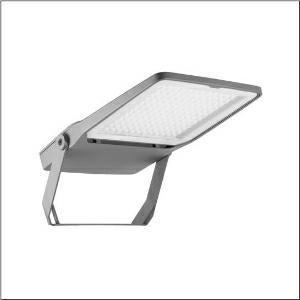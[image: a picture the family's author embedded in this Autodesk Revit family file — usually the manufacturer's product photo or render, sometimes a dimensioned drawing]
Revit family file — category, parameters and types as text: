
# Revit family: floodlight_fl_20_midi___pl52_5xa7682e3d1ac_0316
name_source: partatom
category: Lighting Fixtures
units: mm (PartAtom-declared; Revit-internal decimal feet)

## family parameters
Cut with Voids When Loaded = No
Host = Face
Light Source = No
Part Type = Normal
Room Calculation Point = No
Round Connector Dimension = Use Diameter
Shared = No

## types (1)
- --- (1 x LED 5000K / CRI = 70 (unbekannt), 27250 lm, 5000K)
    Apparent Load = 208 VA
    CIE Flux Codes = 27 59 98 100 100
    Color Rendering = 70
    Color Temperature = 5000K
    Default Elevation = 1800 mm
    Description = Floodlight FL 20 midi, floodlight, primary light control with lens, of plastic, primary optical cover: protective disc, of toughened safety glass, transparent, light distribution: PL52, light emission: direct distribution, primary light characteristic: asymmetric, installation type: surface-mounted, LED High Power LED, rated luminous flux: 27.250 lm, light colour: 750, colour temperature: 5000K, control gear: ECG Plus, control: flexible luminous flux parameterisation, time-dependent luminous flux control, digital communication interface, power reduction, overheat protection, electronic power reduction, with terminal, 5-pole, max. 2.5mm², mains connection: 220..240V, AC, 50/60Hz, rated input power: 208W, LED unit, of diecast aluminium, powder-coated, Siteco® metallic grey (DB 702S), length: 654 mm, width: 450 mm, height: 76mm, housing frame, of diecast aluminium, powder-coated, Siteco® metallic grey (DB 702S), mounting bracket, of steel, powder-coated, Siteco® metallic grey (DB 702S), DALIprotection rating (complete): IP66, insulation class (complete): insulation class II (safety insulation), certification: CE, ENEC, VDE, protection symbol: D, permissible ambient temperature for indoor applications: -40..+40°C, permissible ambient temperature for outdoor applications: -40..+50°C, standard: DIN EN 12944, packaging unit: 1 piece

Light Distribution: PL52
    Height = 76 mm
    Lamp = 1 x LED 5000K / CRI >= 70 (unbekannt)
    Lamp Light Flux = 27250 lm
    Lamp count = 1
    Length = 672 mm
    Luminous efficacy = 131 lm/W
    Manufacturer = Siteco
    ModVariant = No
    Model = 5XA7682E3D1AC
    Number of Poles = 1
    OnlyDefault = Yes
    Power Factor = 1
    Product Name = Floodlight FL 20 midi | PL52
    Product group = floodlight | pylon top
    ProductGroupID = 6101
    Protection Class = Protection class II
    Protection Degree = IP 66
    RLX_Detail_Level = 1
    RlxData = <blob elided: 97557 chars, md5=5200c30d>
    Socket = socket
    Standby Power = 0 W
    System Light Flux = 27250 lm
    System Power = 208 W
    Type Comments = factory setting: luminous flux: 100 % | dim-lin: 254 | 484 mA
    Type Image = l_1005943.jpg
    URL = http://relux.com
    VarID = @adj_142861
    Voltage = 0 V
    Weight = 0.00 kg
    Width = 450 mm

## geometry (parser evidence)
native form markers: Blend x4, Sweep x12
no freeform markers — native parametric forms only
